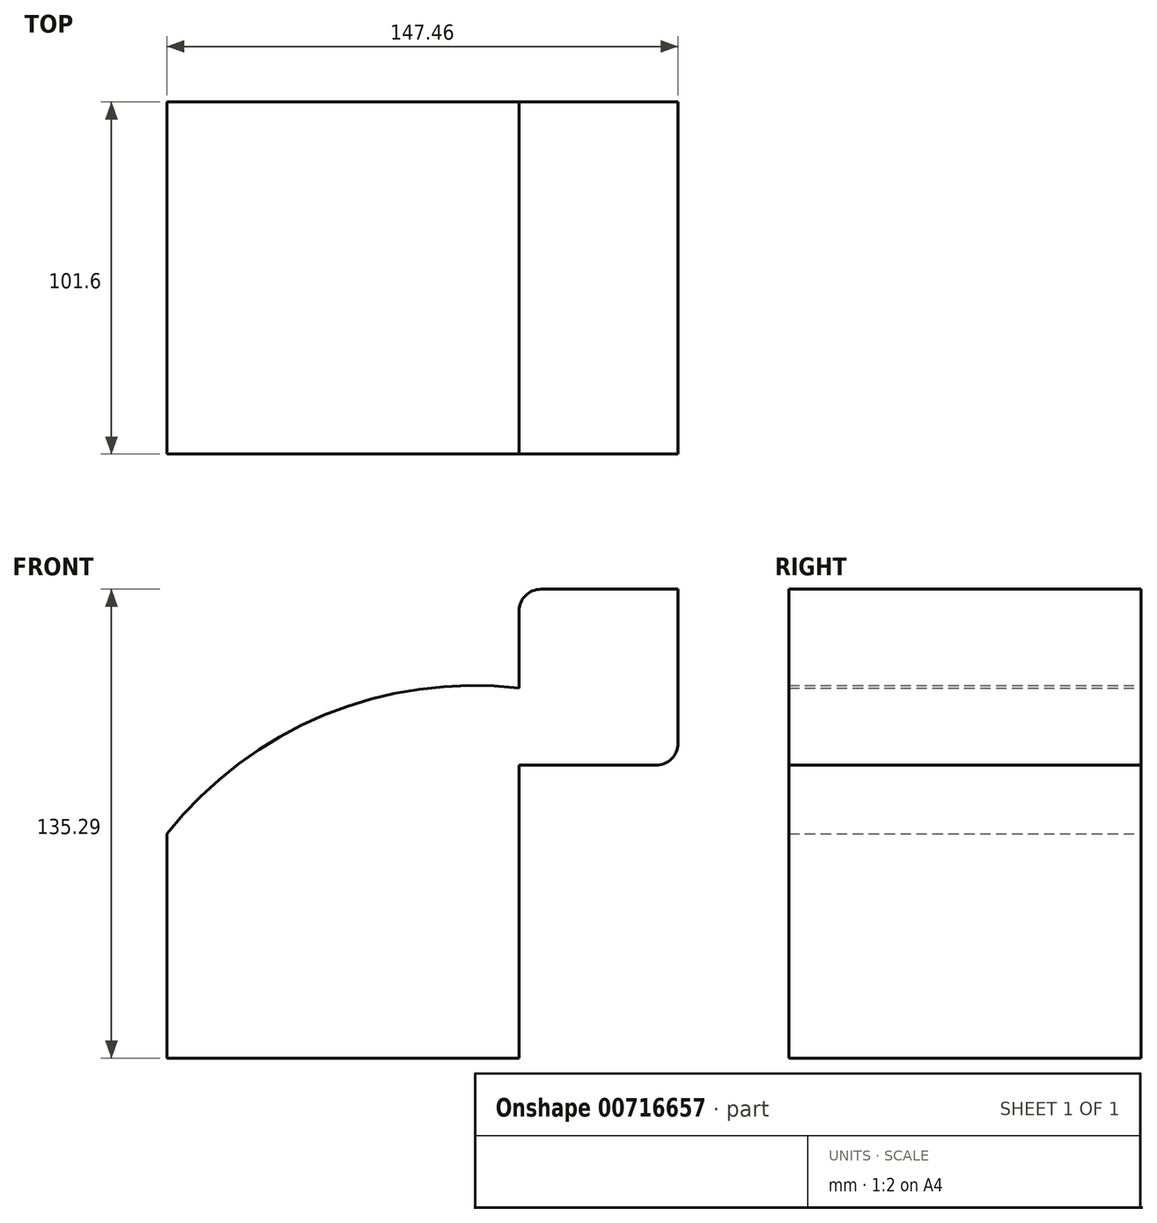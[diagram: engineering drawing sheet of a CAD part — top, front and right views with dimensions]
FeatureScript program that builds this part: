
annotation { "Feature Type Name" : "Feature", "Feature Type Description" : "" }
export const myFeature = defineFeature(function(context is Context, id is Id, definition is map)
    precondition{}
    {
        {
            var Q0;
            Q0=qCreatedBy(makeId("Front.planeOp"),FACE);
            var sketch = newSketch(context, id + "F0", { "sketchPlane" : qUnion([Q0])});
            skLineSegment(sketch, "E0.bottom", {"start": v(50.8, -32.37) * mm, "end": v(-50.8, -32.37) * mm});
            skLineSegment(sketch, "E0.top", {"start": v(50.8, 32.37) * mm, "end": v(-50.8, 32.37) * mm});
            skLineSegment(sketch, "E0.left", {"start": v(50.8, -32.37) * mm, "end": v(50.8, 32.37) * mm});
            skLineSegment(sketch, "E0.right", {"start": v(-50.8, -32.37) * mm, "end": v(-50.8, 32.37) * mm});
            skPoint(sketch, "E0.middle", {"position": v(0, 0) * mm});
            skLineSegment(sketch, "E1.bottom", {"start": v(50.8, 52.12) * mm, "end": v(90.31, 52.12) * mm});
            skLineSegment(sketch, "E1.top", {"start": v(57.15, 102.92) * mm, "end": v(96.66, 102.92) * mm});
            skLineSegment(sketch, "E1.left", {"start": v(50.8, 52.12) * mm, "end": v(50.8, 96.57) * mm});
            skLineSegment(sketch, "E1.right", {"start": v(96.66, 58.47) * mm, "end": v(96.66, 102.92) * mm});
            skPoint(sketch, "E1.middle", {"position": v(73.73, 77.52) * mm});
            skLineSegment(sketch, "E2", {"start": v(50.8, 32.37) * mm, "end": v(50.8, 52.12) * mm});
            skPoint(sketch, "E3.visualSharp", {"position": v(50.8, 102.92) * mm});
            skArc(sketch, "E3.filletArc", {"start": v(57.15, 102.92) * mm, "mid": v(52.66, 101.06) * mm, "end": v(50.8, 96.57) * mm});
            skPoint(sketch, "E4.visualSharp", {"position": v(96.66, 52.12) * mm});
            skArc(sketch, "E4.filletArc", {"start": v(90.31, 52.12) * mm, "mid": v(94.8, 53.98) * mm, "end": v(96.66, 58.47) * mm});
            skArc(sketch, "E5", {"start": v(50.8, 74.35) * mm, "mid": v(24.95, 64.25) * mm, "end": v(14.08, 38.72) * mm});
            skLineSegment(sketch, "E6", {"start": v(14.08, 38.72) * mm, "end": v(14.08, 32.37) * mm});
            skArc(sketch, "E7", {"start": v(50.8, 74.35) * mm, "mid": v(-5.46, 66.57) * mm, "end": v(-50.8, 32.37) * mm});
            skSolve(sketch);
        }
        {
            var Q0;
            Q0=makeQuery(id+"F0.imprint","IMPRINT",FACE,{"disambiguationData":[TD([[makeQuery(id+"F0.imprint","IMPRINT",EDGE,{"derivedFrom":sQuery(id+"F0.wireOp",EDGE,"E0.bottom")}),-1.0]])]});
            var Q1;
            {var subQ1=sQuery(id+"F0.wireOp",EDGE,"E2");Q1=makeQuery(id+"F0.imprint","IMPRINT",FACE,{"disambiguationData":[TD([[makeQuery(id+"F0.imprint","IMPRINT",EDGE,{"derivedFrom":subQ1}),1.0]])]});}
            var Q2;
            Q2=makeQuery(id+"F0.imprint","IMPRINT",FACE,{"disambiguationData":[TD([[makeQuery(id+"F0.imprint","IMPRINT",EDGE,{"derivedFrom":sQuery(id+"F0.wireOp",EDGE,"E5")}),-1.0]])]});
            var Q3;
            {var subQ3=sQuery(id+"F0.wireOp",EDGE,"E1.bottom");Q3=makeQuery(id+"F0.imprint","IMPRINT",FACE,{"disambiguationData":[TD([[makeQuery(id+"F0.imprint","IMPRINT",EDGE,{"derivedFrom":subQ3}),1.0]])]});}
            extrude(context, id + "F1", {"entities" : qUnion([Q0, Q1, Q2, Q3]), "depth" : 101.6 * mm, "offsetDistance" : 25.4 * mm});
        }
    });
